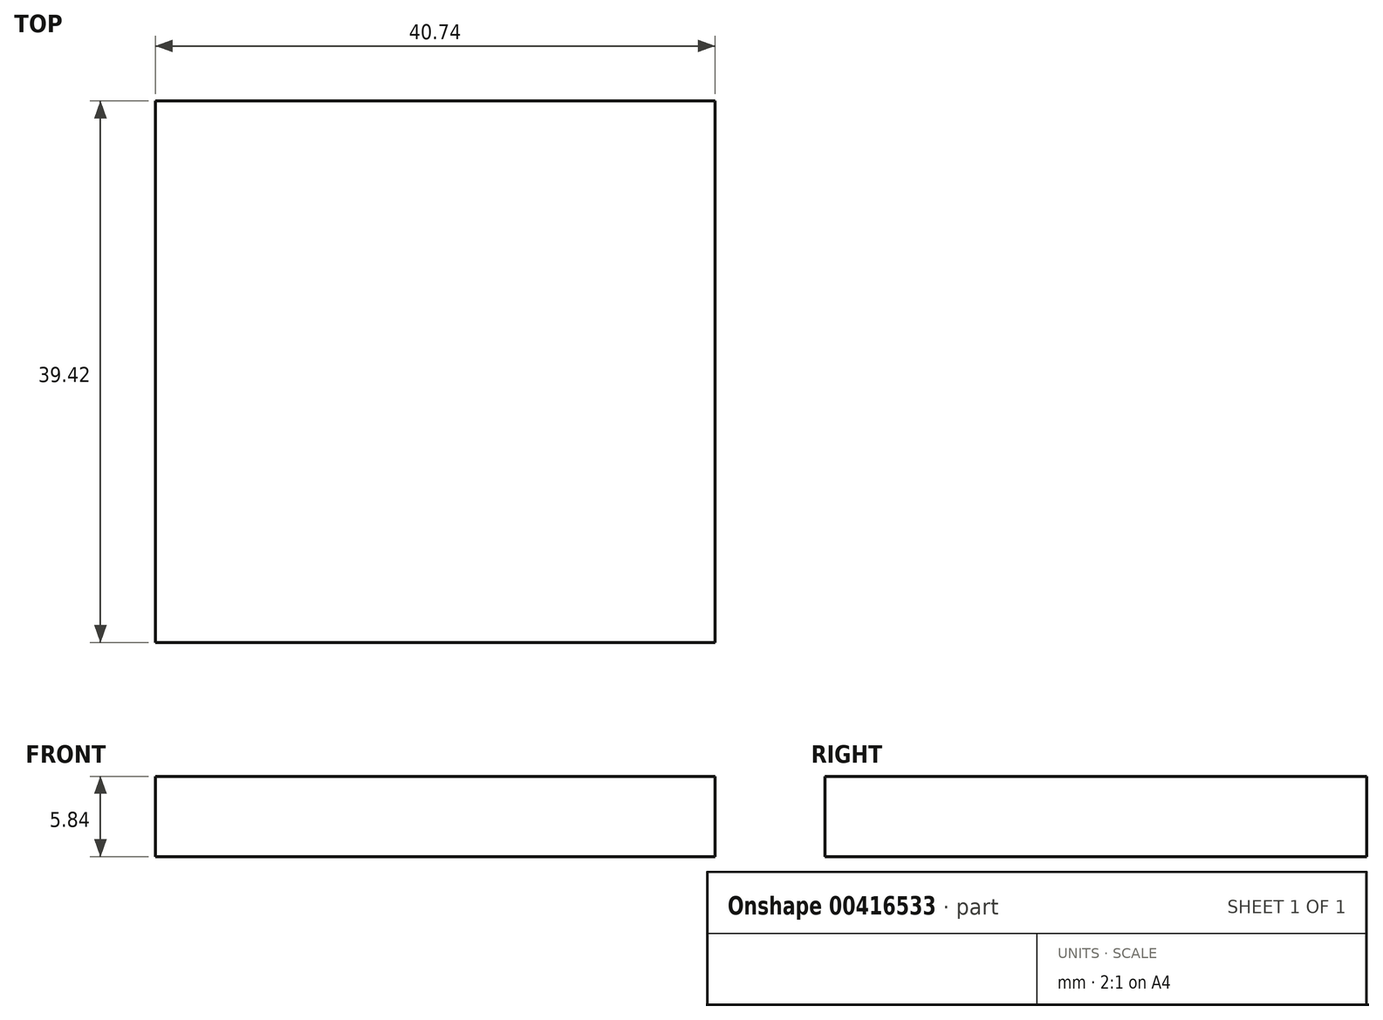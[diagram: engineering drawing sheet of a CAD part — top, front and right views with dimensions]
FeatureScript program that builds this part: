
annotation { "Feature Type Name" : "Feature", "Feature Type Description" : "" }
export const myFeature = defineFeature(function(context is Context, id is Id, definition is map)
    precondition{}
    {
        {
            var Q0;
            Q0=qCreatedBy(makeId("Top.planeOp"),FACE);
            var sketch = newSketch(context, id + "F0", { "sketchPlane" : qUnion([Q0])});
            skLineSegment(sketch, "E0.bottom", {"start": v(0, 0) * mm, "end": v(40.74, 0) * mm});
            skLineSegment(sketch, "E0.top", {"start": v(0, -39.42) * mm, "end": v(40.74, -39.42) * mm});
            skLineSegment(sketch, "E0.left", {"start": v(0, 0) * mm, "end": v(0, -39.42) * mm});
            skLineSegment(sketch, "E0.right", {"start": v(40.74, 0) * mm, "end": v(40.74, -39.42) * mm});
            skSolve(sketch);
        }
        {
            var Q0;
            Q0 = qSketchRegion(id + "F0", true);
            extrude(context, id + "F1", {"entities" : qUnion([Q0]), "depth" : 5.84 * mm});
        }
    });
